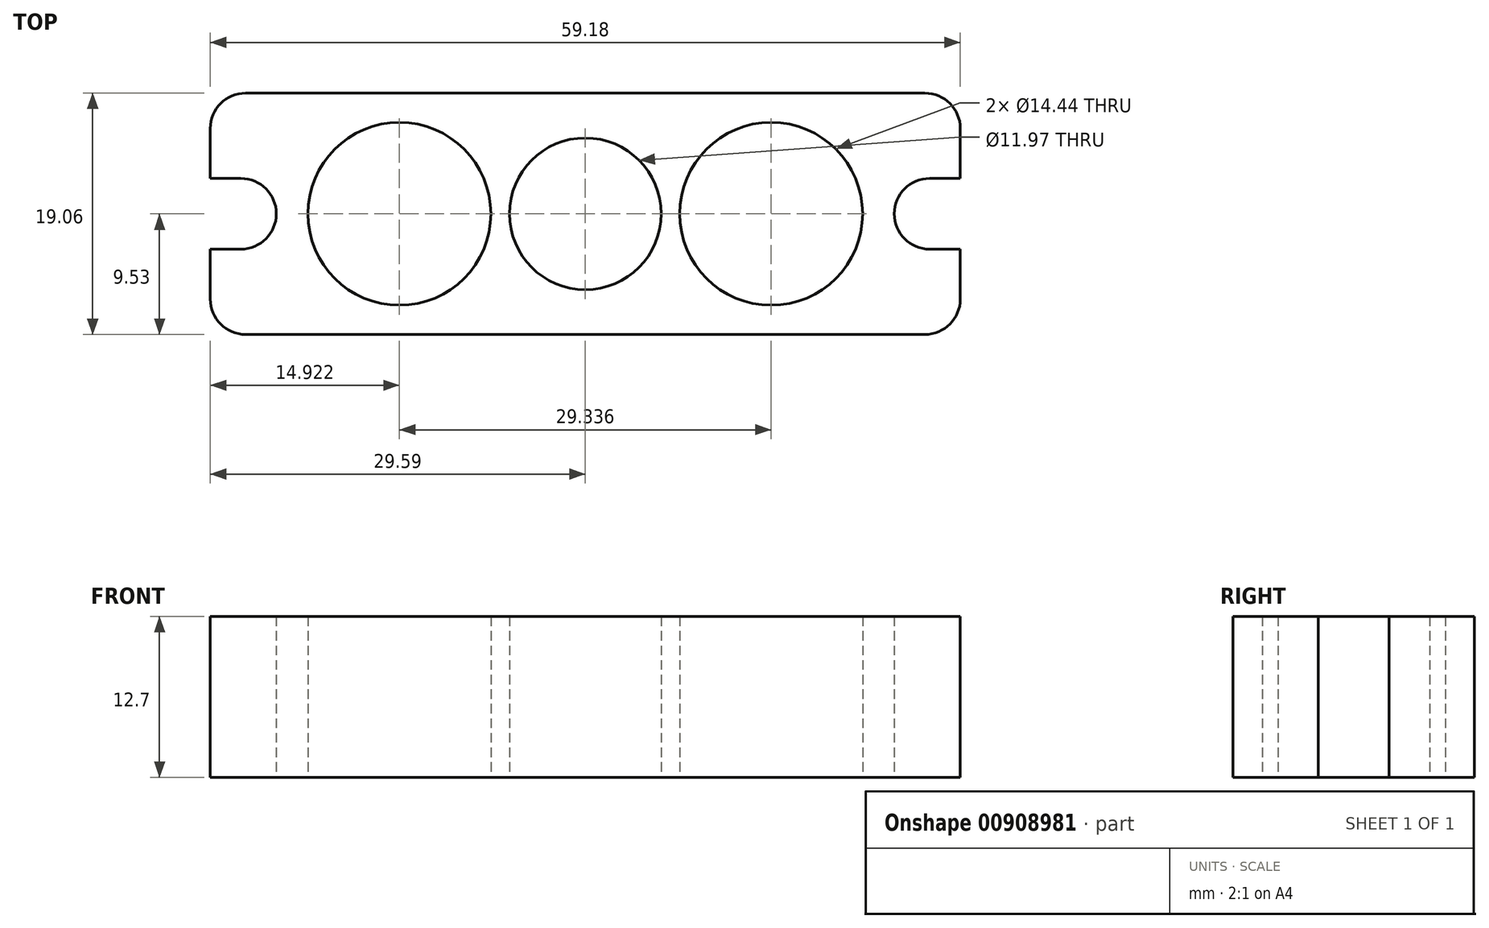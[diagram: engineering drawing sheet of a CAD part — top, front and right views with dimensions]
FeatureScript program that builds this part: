
annotation { "Feature Type Name" : "Feature", "Feature Type Description" : "" }
export const myFeature = defineFeature(function(context is Context, id is Id, definition is map)
    precondition{}
    {
        {
            var Q0;
            Q0=qCreatedBy(makeId("Top.planeOp"),FACE);
            var sketch = newSketch(context, id + "F0", { "sketchPlane" : qUnion([Q0])});
            skLineSegment(sketch, "E0.bottom", {"start": v(-26.8, -9.52) * mm, "end": v(26.8, -9.52) * mm});
            skLineSegment(sketch, "E0.top", {"start": v(-26.8, 9.53) * mm, "end": v(26.8, 9.53) * mm});
            skLineSegment(sketch, "E0.left", {"start": v(-29.6, -6.73) * mm, "end": v(-29.6, -2.8) * mm});
            skLineSegment(sketch, "E0.right", {"start": v(29.6, -6.73) * mm, "end": v(29.6, -2.8) * mm});
            skLineSegment(sketch, "E1", {"start": v(-29.6, 0) * mm, "end": v(29.6, 0) * mm, "construction": true});
            skLineSegment(sketch, "E2.0", {"start": v(27.18, -2.8) * mm, "end": v(29.6, -2.8) * mm});
            skLineSegment(sketch, "E3.0", {"start": v(27.18, 2.8) * mm, "end": v(29.6, 2.8) * mm});
            skArc(sketch, "E4", {"start": v(27.18, 2.8) * mm, "mid": v(24.38, 0) * mm, "end": v(27.18, -2.8) * mm});
            skLineSegment(sketch, "E5.trimOffspring", {"start": v(29.6, 2.8) * mm, "end": v(29.6, 6.73) * mm});
            skLineSegment(sketch, "E6.MirrorCS", {"start": v(-27.18, 2.8) * mm, "end": v(-29.6, 2.8) * mm});
            skLineSegment(sketch, "E7.MirrorCS", {"start": v(-27.18, -2.8) * mm, "end": v(-29.6, -2.8) * mm});
            skArc(sketch, "E8.MirrorCS", {"start": v(-27.18, 2.8) * mm, "mid": v(-24.38, 0) * mm, "end": v(-27.18, -2.8) * mm});
            skLineSegment(sketch, "E9.trimOffspring", {"start": v(-29.6, 2.8) * mm, "end": v(-29.6, 6.73) * mm});
            skPoint(sketch, "E10.visualSharp", {"position": v(-29.6, 9.52) * mm});
            skArc(sketch, "E10.filletArc", {"start": v(-26.8, 9.52) * mm, "mid": v(-28.77, 8.7) * mm, "end": v(-29.6, 6.73) * mm});
            skPoint(sketch, "E11.visualSharp", {"position": v(29.6, 9.53) * mm});
            skArc(sketch, "E11.filletArc", {"start": v(29.6, 6.73) * mm, "mid": v(28.77, 8.7) * mm, "end": v(26.8, 9.52) * mm});
            skPoint(sketch, "E12.visualSharp", {"position": v(29.6, -9.52) * mm});
            skArc(sketch, "E12.filletArc", {"start": v(26.8, -9.52) * mm, "mid": v(28.77, -8.7) * mm, "end": v(29.6, -6.73) * mm});
            skPoint(sketch, "E13.visualSharp", {"position": v(-29.6, -9.52) * mm});
            skArc(sketch, "E13.filletArc", {"start": v(-29.6, -6.73) * mm, "mid": v(-28.77, -8.7) * mm, "end": v(-26.8, -9.52) * mm});
            skCircle(sketch, "E14", {"center": v(0, 0) * mm, "radius": 5.98 * mm});
            skCircle(sketch, "E15", {"center": v(14.67, 0) * mm, "radius": 7.22 * mm});
            skCircle(sketch, "E16.MirrorC", {"center": v(-14.67, 0) * mm, "radius": 7.22 * mm});
            skSolve(sketch);
        }
        {
            var Q0;
            Q0=makeQuery(id+"F0.imprint","IMPRINT",FACE,{"disambiguationData":[TD([[makeQuery(id+"F0.imprint","IMPRINT",EDGE,{"derivedFrom":sQuery(id+"F0.wireOp",EDGE,"E0.bottom")}),1.0]])]});
            extrude(context, id + "F1", {"entities" : qUnion([Q0]), "depth" : 12.7 * mm, "offsetDistance" : 25.4 * mm});
        }
    });
